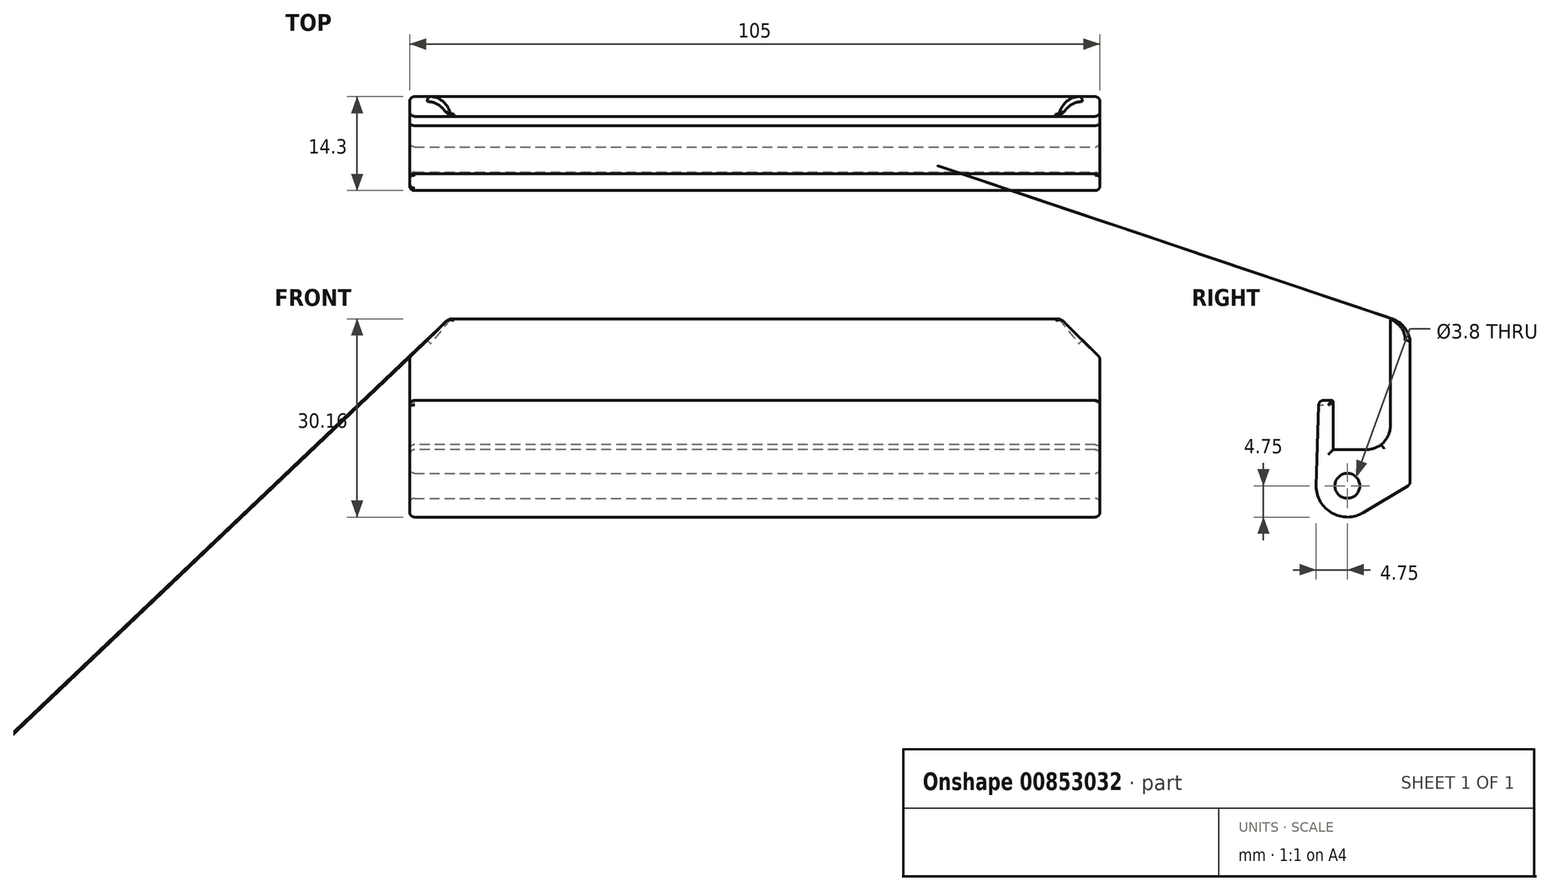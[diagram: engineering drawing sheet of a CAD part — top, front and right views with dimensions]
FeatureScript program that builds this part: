
annotation { "Feature Type Name" : "Feature", "Feature Type Description" : "" }
export const myFeature = defineFeature(function(context is Context, id is Id, definition is map)
    precondition{}
    {
        {
            var Q0;
            Q0=qCreatedBy(makeId("Right.planeOp"),FACE);
            var sketch = newSketch(context, id + "F0", { "sketchPlane" : qUnion([Q0])});
            skArc(sketch, "E0", {"start": v(-4.75, 0) * mm, "mid": v(-2.34, -4.13) * mm, "end": v(2.45, -4.07) * mm});
            skLineSegment(sketch, "E1", {"start": v(-4.75, 0) * mm, "end": v(-4.35, 13) * mm});
            skLineSegment(sketch, "E2", {"start": v(-4.35, 13) * mm, "end": v(-2.15, 13) * mm});
            skLineSegment(sketch, "E3", {"start": v(-2.15, 13) * mm, "end": v(-2.15, 5.5) * mm});
            skLineSegment(sketch, "E4", {"start": v(-2.15, 5.5) * mm, "end": v(4.19, 5.5) * mm});
            skLineSegment(sketch, "E5", {"start": v(6.55, 7.35) * mm, "end": v(6.55, 25.5) * mm});
            skLineSegment(sketch, "E6", {"start": v(9.55, 25.5) * mm, "end": v(9.55, 0.2) * mm});
            skLineSegment(sketch, "E7", {"start": v(6.55, 7.35) * mm, "end": v(4.19, 5.5) * mm});
            skLineSegment(sketch, "E8", {"start": v(9.55, 25.5) * mm, "end": v(6.55, 25.5) * mm});
            skLineSegment(sketch, "E9", {"start": v(0, 0) * mm, "end": v(30.48, 0) * mm, "construction": true});
            skLineSegment(sketch, "E10", {"start": v(2.45, -4.07) * mm, "end": v(9.55, 0.2) * mm});
            skSolve(sketch);
        }
        {
            var Q0;
            Q0 = qSketchRegion(id + "F0", true);
            extrude(context, id + "F1", {"entities" : qUnion([Q0]), "depth" : (130 - 24 - 1) * mm, "offsetDistance" : 25 * mm, "symmetric" : true});
        }
        {
            var Q0;
            Q0=makeQuery(id+"F1.opExtrude","CAP_FACE",FACE,{"disambiguationData":[OSD([sQuery(id+"F0.wireOp",EDGE,"E0"),sQuery(id+"F0.wireOp",EDGE,"E1"),sQuery(id+"F0.wireOp",EDGE,"E2"),sQuery(id+"F0.wireOp",EDGE,"E3"),sQuery(id+"F0.wireOp",EDGE,"E4"),sQuery(id+"F0.wireOp",EDGE,"E5"),sQuery(id+"F0.wireOp",EDGE,"E6"),sQuery(id+"F0.wireOp",EDGE,"E7"),sQuery(id+"F0.wireOp",EDGE,"E8"),sQuery(id+"F0.wireOp",EDGE,"E10")])],"isStart":false});
            var sketch = newSketch(context, id + "F2", { "sketchPlane" : qUnion([Q0])});
            skCircle(sketch, "E11", {"center": v(0, 0) * mm, "radius": 1.9 * mm});
            skSolve(sketch);
        }
        {
            var Q0;
            Q0=makeQuery(id+"F2.imprint","IMPRINT",FACE,{"disambiguationData":[TD([[makeQuery(id+"F2.imprint","IMPRINT",EDGE,{"derivedFrom":sQuery(id+"F2.wireOp",EDGE,"E11")}),1.0]])]});
            extrude(context, id + "F3", {"entities" : qUnion([Q0]), "operationType" : NewBodyOperationType.REMOVE, "endBound" : BoundingType.THROUGH_ALL, "oppositeDirection" : true, "depth" : 25 * mm, "offsetDistance" : 25 * mm});
        }
        {
            var Q0;
            Q0=makeQuery(id+"F1.opExtrude","CAP_EDGE",EDGE,{"disambiguationData":[OSD([sQuery(id+"F0.wireOp",EDGE,"E8")])],"isStart":false});
            var Q1;
            Q1=makeQuery(id+"F1.opExtrude","CAP_EDGE",EDGE,{"disambiguationData":[OSD([sQuery(id+"F0.wireOp",EDGE,"E8")])],"isStart":true});
            chamfer(context, id + "F4", {"entities" : qUnion([Q0, Q1]), "width" : 6 * mm, "tangentPropagation" : true});
        }
        {
            var Q0;
            Q0=makeQuery(id+"F1.opExtrude","SWEPT_EDGE",EDGE,{"disambiguationData":[OSD([sQuery(id+"F0.wireOp",EDGE,"E4"),sQuery(id+"F0.wireOp",EDGE,"E7")])]});
            var Q1;
            Q1=makeQuery(id+"F1.opExtrude","SWEPT_EDGE",EDGE,{"disambiguationData":[OSD([sQuery(id+"F0.wireOp",EDGE,"E5"),sQuery(id+"F0.wireOp",EDGE,"E7")])]});
            var Q2;
            Q2=makeQuery(id+"F1.opExtrude","SWEPT_EDGE",EDGE,{"disambiguationData":[OSD([sQuery(id+"F0.wireOp",EDGE,"E6"),sQuery(id+"F0.wireOp",EDGE,"E8")])]});
            fillet(context, id + "F5", {"entities" : qUnion([Q0, Q1, Q2]), "radius" : 4 * mm, "tangentPropagation" : true, "allowEdgeOverflow" : false});
        }
        {
            var Q0;
            Q0=makeQuery(id+"F1.opExtrude","SWEPT_EDGE",EDGE,{"disambiguationData":[OSD([sQuery(id+"F0.wireOp",EDGE,"E0"),sQuery(id+"F0.wireOp",EDGE,"E1")])]});
            var Q1;
            Q1=makeQuery(id+"F1.opExtrude","SWEPT_EDGE",EDGE,{"disambiguationData":[OSD([sQuery(id+"F0.wireOp",EDGE,"E1"),sQuery(id+"F0.wireOp",EDGE,"E2")])]});
            var Q2;
            Q2=makeQuery(id+"F1.opExtrude","SWEPT_EDGE",EDGE,{"disambiguationData":[OSD([sQuery(id+"F0.wireOp",EDGE,"E6"),sQuery(id+"F0.wireOp",EDGE,"E10")])]});
            var Q3;
            Q3=makeQuery(id+"F1.opExtrude","CAP_FACE",FACE,{"disambiguationData":[OSD([sQuery(id+"F0.wireOp",EDGE,"E0"),sQuery(id+"F0.wireOp",EDGE,"E1"),sQuery(id+"F0.wireOp",EDGE,"E2"),sQuery(id+"F0.wireOp",EDGE,"E3"),sQuery(id+"F0.wireOp",EDGE,"E4"),sQuery(id+"F0.wireOp",EDGE,"E5"),sQuery(id+"F0.wireOp",EDGE,"E6"),sQuery(id+"F0.wireOp",EDGE,"E7"),sQuery(id+"F0.wireOp",EDGE,"E8"),sQuery(id+"F0.wireOp",EDGE,"E10")])],"isStart":false});
            var Q4;
            {var subQ0=sQuery(id+"F0.wireOp",EDGE,"E8");Q4=makeQuery(id+"F4.opChamfer","BLEND_FACE",FACE,{"disambiguationData":[OSD([subQ0]),TDD([makeQuery(id+"F1.opExtrude","CAP_EDGE",EDGE,{"disambiguationData":[OSD([subQ0])],"isStart":false})])]});}
            var Q5;
            Q5=makeQuery(id+"F1.opExtrude","CAP_FACE",FACE,{"disambiguationData":[OSD([sQuery(id+"F0.wireOp",EDGE,"E0"),sQuery(id+"F0.wireOp",EDGE,"E1"),sQuery(id+"F0.wireOp",EDGE,"E2"),sQuery(id+"F0.wireOp",EDGE,"E3"),sQuery(id+"F0.wireOp",EDGE,"E4"),sQuery(id+"F0.wireOp",EDGE,"E5"),sQuery(id+"F0.wireOp",EDGE,"E6"),sQuery(id+"F0.wireOp",EDGE,"E7"),sQuery(id+"F0.wireOp",EDGE,"E8"),sQuery(id+"F0.wireOp",EDGE,"E10")])],"isStart":true});
            var Q6;
            {var subQ0=sQuery(id+"F0.wireOp",EDGE,"E8");Q6=makeQuery(id+"F4.opChamfer","BLEND_FACE",FACE,{"disambiguationData":[OSD([subQ0]),TDD([makeQuery(id+"F1.opExtrude","CAP_EDGE",EDGE,{"disambiguationData":[OSD([subQ0])],"isStart":true})])]});}
            fillet(context, id + "F6", {"entities" : qUnion([Q0, Q1, Q2, Q3, Q4, Q5, Q6]), "radius" : 0.75 * mm, "tangentPropagation" : true, "allowEdgeOverflow" : false});
        }
        {
            var Q0;
            Q0=makeQuery(id+"F1.opExtrude","SWEPT_EDGE",EDGE,{"disambiguationData":[OSD([sQuery(id+"F0.wireOp",EDGE,"E2"),sQuery(id+"F0.wireOp",EDGE,"E3")])]});
            var Q1;
            Q1=makeQuery(id+"F5.opFillet","BLEND_EDGE",EDGE,{"blendedFrom":[makeQuery(id+"F1.opExtrude","SWEPT_EDGE",EDGE,{"disambiguationData":[OSD([sQuery(id+"F0.wireOp",EDGE,"E6"),sQuery(id+"F0.wireOp",EDGE,"E8")])]}),makeQuery(id+"F1.opExtrude","SWEPT_FACE",FACE,{"disambiguationData":[OSD([sQuery(id+"F0.wireOp",EDGE,"E5")])]})],"blendedInto":[makeQuery(id+"F1.opExtrude","SWEPT_FACE",FACE,{"disambiguationData":[OSD([sQuery(id+"F0.wireOp",EDGE,"E5")])]})]});
            fillet(context, id + "F7", {"entities" : qUnion([Q0, Q1]), "radius" : 0.25 * mm, "tangentPropagation" : true, "allowEdgeOverflow" : false});
        }
    });
